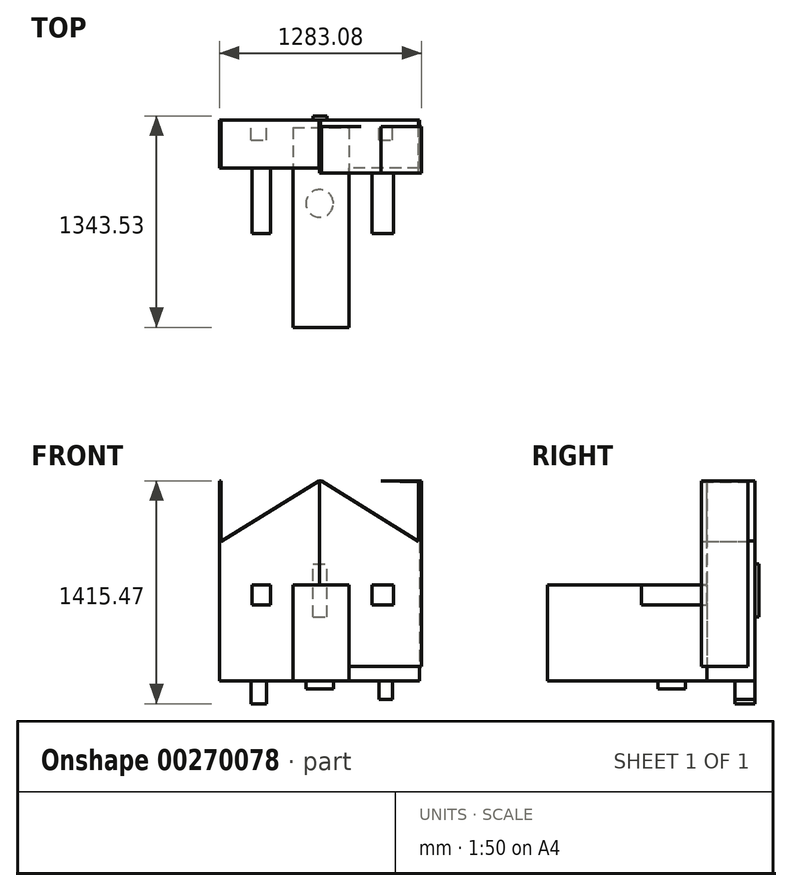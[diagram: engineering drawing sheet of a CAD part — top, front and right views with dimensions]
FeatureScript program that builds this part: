
annotation { "Feature Type Name" : "Feature", "Feature Type Description" : "" }
export const myFeature = defineFeature(function(context is Context, id is Id, definition is map)
    precondition{}
    {
        {
            var Q0;
            Q0=qCreatedBy(makeId("Front.planeOp"),FACE);
            var sketch = newSketch(context, id + "F0", { "sketchPlane" : qUnion([Q0])});
            skLineSegment(sketch, "E0.bottom", {"start": v(-635.38, 660.7) * mm, "end": v(634.62, 660.7) * mm});
            skLineSegment(sketch, "E0.top", {"start": v(-635.38, -609.3) * mm, "end": v(634.62, -609.3) * mm});
            skLineSegment(sketch, "E0.left", {"start": v(-635.38, 660.7) * mm, "end": v(-635.38, -609.3) * mm});
            skLineSegment(sketch, "E0.right", {"start": v(634.62, 660.7) * mm, "end": v(634.62, -609.3) * mm});
            skSolve(sketch);
        }
        {
            var Q0;
            Q0 = qSketchRegion(id + "F0", true);
            extrude(context, id + "F1", {"entities" : qUnion([Q0]), "depth" : 304.8 * mm});
        }
        {
            var Q0;
            Q0=qCreatedBy(makeId("Top.planeOp"),FACE);
            var sketch = newSketch(context, id + "F2", { "sketchPlane" : qUnion([Q0])});
            skLineSegment(sketch, "E1.bottom", {"start": v(-169.41, -48.13) * mm, "end": v(185.76, -48.13) * mm});
            skLineSegment(sketch, "E1.top", {"start": v(-169.41, -1318.13) * mm, "end": v(185.76, -1318.13) * mm});
            skLineSegment(sketch, "E1.left", {"start": v(-169.41, -48.13) * mm, "end": v(-169.41, -1318.13) * mm});
            skLineSegment(sketch, "E1.right", {"start": v(185.76, -48.13) * mm, "end": v(185.76, -1318.13) * mm});
            skSolve(sketch);
        }
        {
            var Q0;
            Q0 = qSketchRegion(id + "F2", true);
            extrude(context, id + "F3", {"entities" : qUnion([Q0]), "operationType" : NewBodyOperationType.ADD, "oppositeDirection" : true, "depth" : 609.6 * mm});
        }
        {
            var Q0;
            Q0=qCreatedBy(makeId("Top.planeOp"),FACE);
            var sketch = newSketch(context, id + "F4", { "sketchPlane" : qUnion([Q0])});
            skCircle(sketch, "E2", {"center": v(0, -530.93) * mm, "radius": 87.32 * mm});
            skSolve(sketch);
        }
        {
            var Q0;
            Q0 = qSketchRegion(id + "F4", true);
            extrude(context, id + "F5", {"entities" : qUnion([Q0]), "operationType" : NewBodyOperationType.ADD, "oppositeDirection" : true, "depth" : 660.4 * mm});
        }
        {
            var Q0;
            Q0=qCreatedBy(makeId("Front.planeOp"),FACE);
            var sketch = newSketch(context, id + "F6", { "sketchPlane" : qUnion([Q0])});
            skLineSegment(sketch, "E3.bottom", {"start": v(376.27, -312.96) * mm, "end": v(462.48, -312.96) * mm});
            skLineSegment(sketch, "E3.top", {"start": v(376.27, -727.83) * mm, "end": v(462.48, -727.83) * mm});
            skLineSegment(sketch, "E3.left", {"start": v(376.27, -312.96) * mm, "end": v(376.27, -727.83) * mm});
            skLineSegment(sketch, "E3.right", {"start": v(462.48, -312.96) * mm, "end": v(462.48, -727.83) * mm});
            skLineSegment(sketch, "E4.bottom", {"start": v(-337.65, -312.96) * mm, "end": v(-434.63, -312.96) * mm});
            skLineSegment(sketch, "E4.top", {"start": v(-337.65, -754.77) * mm, "end": v(-434.63, -754.77) * mm});
            skLineSegment(sketch, "E4.left", {"start": v(-337.65, -312.96) * mm, "end": v(-337.65, -754.77) * mm});
            skLineSegment(sketch, "E4.right", {"start": v(-434.63, -312.96) * mm, "end": v(-434.63, -754.77) * mm});
            skSolve(sketch);
        }
        {
            var Q0;
            Q0 = qSketchRegion(id + "F6", true);
            extrude(context, id + "F7", {"entities" : qUnion([Q0]), "operationType" : NewBodyOperationType.ADD, "depth" : 127 * mm});
        }
        {
            var Q0;
            Q0=qCreatedBy(makeId("Top.planeOp"),FACE);
            var sketch = newSketch(context, id + "F8", { "sketchPlane" : qUnion([Q0])});
            skLineSegment(sketch, "E5.bottom", {"start": v(469.69, -722.48) * mm, "end": v(333.73, -722.48) * mm});
            skLineSegment(sketch, "E5.top", {"start": v(469.69, -70.73) * mm, "end": v(333.73, -70.73) * mm});
            skLineSegment(sketch, "E5.left", {"start": v(469.69, -722.48) * mm, "end": v(469.69, -70.73) * mm});
            skLineSegment(sketch, "E5.right", {"start": v(333.73, -722.48) * mm, "end": v(333.73, -70.73) * mm});
            skLineSegment(sketch, "E6.bottom", {"start": v(-311.46, -722.48) * mm, "end": v(-428.98, -722.48) * mm});
            skLineSegment(sketch, "E6.top", {"start": v(-311.46, -100.06) * mm, "end": v(-428.98, -100.06) * mm});
            skLineSegment(sketch, "E6.left", {"start": v(-311.46, -722.48) * mm, "end": v(-311.46, -100.06) * mm});
            skLineSegment(sketch, "E6.right", {"start": v(-428.98, -722.48) * mm, "end": v(-428.98, -100.06) * mm});
            skSolve(sketch);
        }
        {
            var Q0;
            Q0 = qSketchRegion(id + "F8", true);
            extrude(context, id + "F9", {"entities" : qUnion([Q0]), "operationType" : NewBodyOperationType.ADD, "oppositeDirection" : true, "depth" : 127 * mm});
        }
        {
            var Q0;
            Q0=qCreatedBy(makeId("Front.planeOp"),FACE);
            var sketch = newSketch(context, id + "F10", { "sketchPlane" : qUnion([Q0])});
            skLineSegment(sketch, "E7", {"start": v(634.54, 274.27) * mm, "end": v(0, 663.46) * mm});
            skLineSegment(sketch, "E8", {"start": v(0, 663.46) * mm, "end": v(643.66, 663.46) * mm});
            skLineSegment(sketch, "E9", {"start": v(643.66, 663.46) * mm, "end": v(634.54, 274.27) * mm});
            skLineSegment(sketch, "E10", {"start": v(0, 663.46) * mm, "end": v(-627.27, 274.27) * mm});
            skLineSegment(sketch, "E11", {"start": v(-627.27, 274.27) * mm, "end": v(-627.27, 663.46) * mm});
            skLineSegment(sketch, "E12", {"start": v(-627.27, 663.46) * mm, "end": v(0, 663.46) * mm});
            skSolve(sketch);
        }
        {
            var Q0;
            Q0 = qSketchRegion(id + "F10", true);
            extrude(context, id + "F11", {"entities" : qUnion([Q0]), "operationType" : NewBodyOperationType.REMOVE, "depth" : 381 * mm});
        }
        {
            var Q0;
            Q0=qCreatedBy(makeId("Front.planeOp"),FACE);
            var sketch = newSketch(context, id + "F12", { "sketchPlane" : qUnion([Q0])});
            skLineSegment(sketch, "E13.bottom", {"start": v(-41.86, -204.88) * mm, "end": v(48, -204.88) * mm});
            skLineSegment(sketch, "E13.top", {"start": v(-41.86, 131.54) * mm, "end": v(48, 131.54) * mm});
            skLineSegment(sketch, "E13.left", {"start": v(-41.86, -204.88) * mm, "end": v(-41.86, 131.54) * mm});
            skLineSegment(sketch, "E13.right", {"start": v(48, -204.88) * mm, "end": v(48, 131.54) * mm});
            skSolve(sketch);
        }
        {
            var Q0;
            Q0 = qSketchRegion(id + "F12", true);
            extrude(context, id + "F13", {"entities" : qUnion([Q0]), "operationType" : NewBodyOperationType.ADD, "oppositeDirection" : true, "depth" : 25.4 * mm});
        }
        {
            var Q0;
            Q0=qCreatedBy(makeId("Right.planeOp"),FACE);
            var sketch = newSketch(context, id + "F14", { "sketchPlane" : qUnion([Q0])});
            skLineSegment(sketch, "E14.bottom", {"start": v(-339.2, -516.72) * mm, "end": v(-43.92, -516.72) * mm});
            skLineSegment(sketch, "E14.top", {"start": v(-339.2, 658.99) * mm, "end": v(-43.92, 658.99) * mm});
            skLineSegment(sketch, "E14.left", {"start": v(-339.2, -516.72) * mm, "end": v(-339.2, 658.99) * mm});
            skLineSegment(sketch, "E14.right", {"start": v(-43.92, -516.72) * mm, "end": v(-43.92, 658.99) * mm});
            skSolve(sketch);
        }
        {
            var Q0;
            Q0 = qSketchRegion(id + "F14", true);
            extrude(context, id + "F15", {"entities" : qUnion([Q0]), "operationType" : NewBodyOperationType.ADD, "depth" : 647.7 * mm});
        }
        {
            var Q0;
            Q0=qCreatedBy(makeId("Front.planeOp"),FACE);
            var sketch = newSketch(context, id + "F16", { "sketchPlane" : qUnion([Q0])});
            skLineSegment(sketch, "E15", {"start": v(0, 666.13) * mm, "end": v(628.3, 274.4) * mm});
            skLineSegment(sketch, "E16", {"start": v(628.3, 274.4) * mm, "end": v(628.3, 654.61) * mm});
            skLineSegment(sketch, "E17", {"start": v(628.3, 654.61) * mm, "end": v(0, 666.13) * mm});
            skSolve(sketch);
        }
        {
            var Q0;
            Q0 = qSketchRegion(id + "F16", true);
            extrude(context, id + "F17", {"entities" : qUnion([Q0]), "operationType" : NewBodyOperationType.REMOVE, "depth" : 508 * mm});
        }
    });
